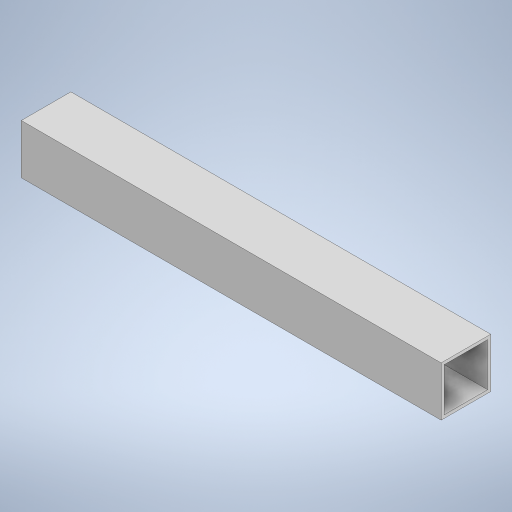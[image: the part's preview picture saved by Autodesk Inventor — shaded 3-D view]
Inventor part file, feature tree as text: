
AUTODESK INVENTOR PART (.ipt)
format: ipt  version: 2024 (Build 280153000, 153)  size: 223,744 bytes
history: native  units: in
note: dims shown in document units (in); Inventor stores cm internally (conversion verified against a paired STEP export)
features: extrude x1, sketch x1
ambient origin geometry x8: Origin, YZ Plane, XZ Plane, XY Plane, X Axis, Y Axis, Z Axis, Center Point
bodies: Solid1 (feature_tree)
feature tree (2):
  extrude  "Extrusion1"  Depth=1.0in
  sketch  "Sketch1"  dims[d0=1.0in d1=1.0in d2=0.0625in d3=8.4646in d4=0.0in d5=0.5in d6=0.0344in d7=0.5in d8=0.0344in]
